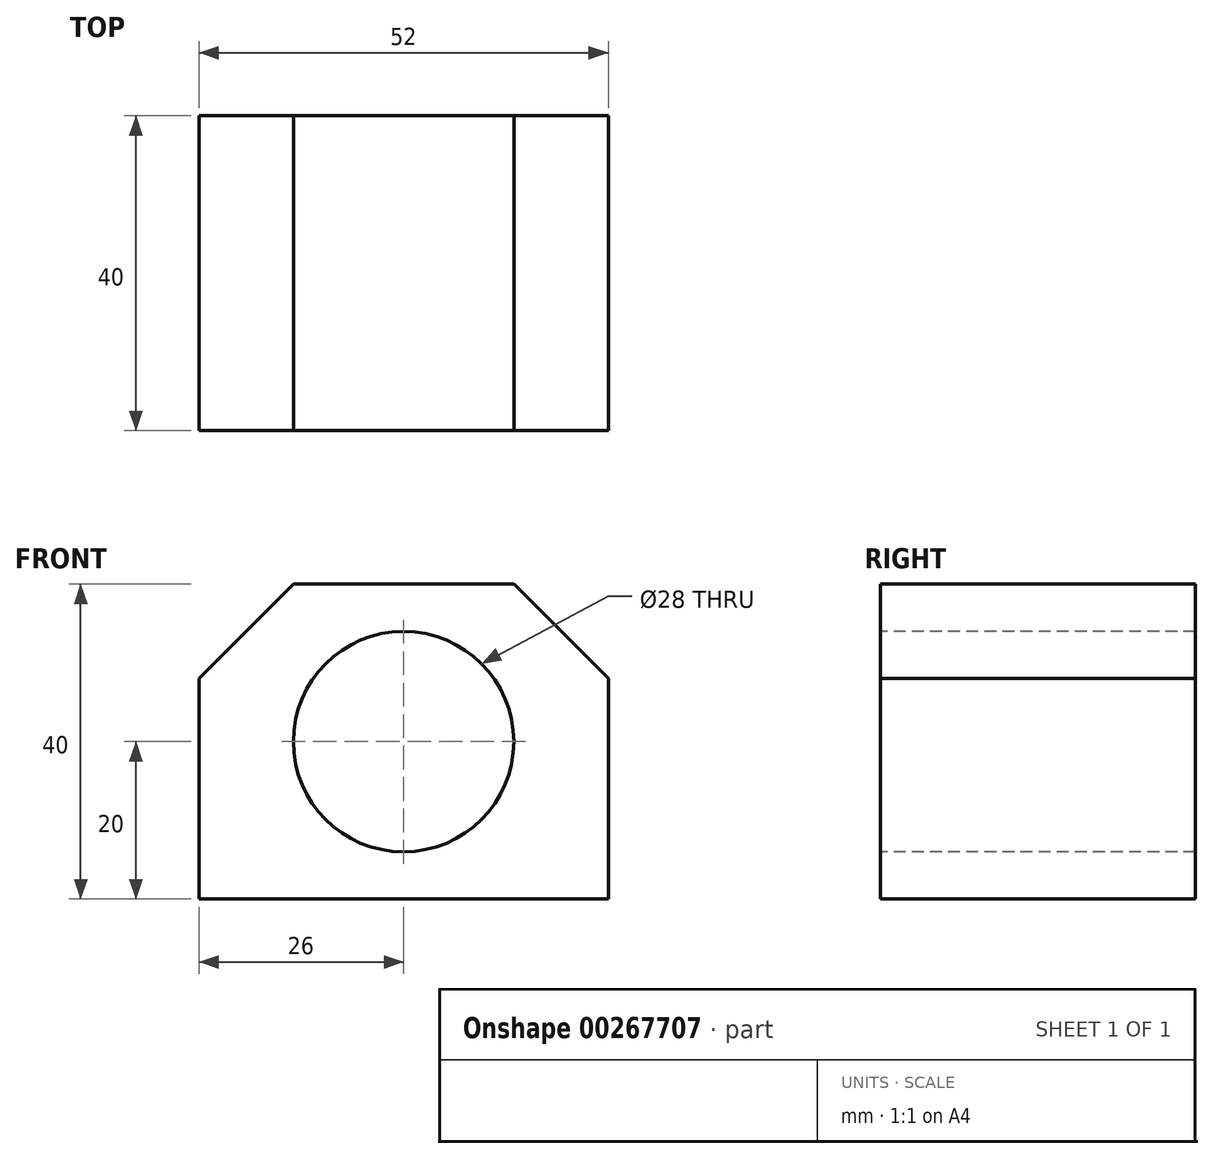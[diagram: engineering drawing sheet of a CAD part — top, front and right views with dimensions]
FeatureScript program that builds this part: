
annotation { "Feature Type Name" : "Feature", "Feature Type Description" : "" }
export const myFeature = defineFeature(function(context is Context, id is Id, definition is map)
    precondition{}
    {
        {
            var Q0;
            Q0=qCreatedBy(makeId("Front.planeOp"),FACE);
            var sketch = newSketch(context, id + "F0", { "sketchPlane" : qUnion([Q0])});
            skLineSegment(sketch, "E0.bottom", {"start": v(-14, 20) * mm, "end": v(14, 20) * mm});
            skLineSegment(sketch, "E0.top", {"start": v(-26, -20) * mm, "end": v(26, -20) * mm});
            skLineSegment(sketch, "E0.left", {"start": v(-26, 8) * mm, "end": v(-26, -20) * mm});
            skLineSegment(sketch, "E0.right", {"start": v(26, 8) * mm, "end": v(26, -20) * mm});
            skPoint(sketch, "E0.middle", {"position": v(0, 0) * mm});
            skLineSegment(sketch, "E1", {"start": v(-26, 8) * mm, "end": v(-14, 20) * mm});
            skLineSegment(sketch, "E2", {"start": v(14, 20) * mm, "end": v(26, 8) * mm});
            skPoint(sketch, "E3.orphan", {"position": v(-26, 20) * mm});
            skPoint(sketch, "E4.orphan", {"position": v(26, 20) * mm});
            skCircle(sketch, "E5", {"center": v(0, 0) * mm, "radius": 14 * mm});
            skSolve(sketch);
        }
        {
            var Q0;
            Q0=qSketchRegion(id+"F0",true);
            extrude(context, id + "F1", {"entities" : qUnion([Q0]), "oppositeDirection" : true, "depth" : 40 * mm});
        }
    });
